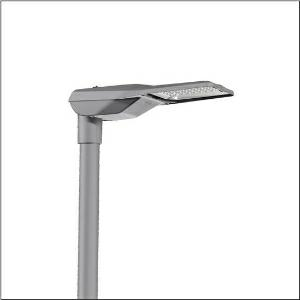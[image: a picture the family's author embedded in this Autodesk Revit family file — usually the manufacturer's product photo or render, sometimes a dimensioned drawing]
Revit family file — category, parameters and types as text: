
# Revit family: streetlight_sl_21_mini___p1_0a_5xe2a43s08gb_f3ee
name_source: partatom
category: Lighting Fixtures
units: mm (PartAtom-declared; Revit-internal decimal feet)

## family parameters
Cut with Voids When Loaded = No
Host = Face
Light Source = No
Part Type = Normal
Room Calculation Point = No
Round Connector Dimension = Use Diameter
Shared = No

## types (1)
- --- (1 x LED, 6180 lm, 40.4 W, 4000K)
    Apparent Load = 40 VA
    CIE Flux Codes = 21 50 90 100 100
    Color Rendering = 70
    Color Temperature = 4000K
    Default Elevation = 1800 mm
    Description = Streetlight SL 21 mini, mast luminaire, primary light control with lens, of PMMA, primary optical cover: cover, of toughened safety glass, transparent, light distribution: P1.0a, light emission: direct distribution, primary light characteristic: asymmetric, installation type: side-entry, post-top, LED, High Power LED, rated luminous flux: 6.180lm, luminous efficacy: 153lm/W, light colour: 740, colour temperature: 4000K, control gear: ECG Smart Interface, control: overheat protection, constant luminous flux control, time-dependent luminous flux control, flexible luminous flux parameterisation, mains connection: 220..240V, AC, 50/60Hz, start of lifetime: 40W, end of lifetime: 41W, reduction: 19W, luminaire housing, of diecast aluminium, powder-coated, Siteco® metallic grey (DB 702S), corrosivity category C5 according to DIN EN ISO 12944, length: 628mm, width: 235mm, height: 110mm, spigot size: 60/76mm (post-top) and 42/60/76mm (side-entry), mast flange for spigot size: 42mm: 5XC10008XM4, 60mm: 5XC10008XM2, 76/60mm: 5XC10108XM1, protection rating (complete): IP66, insulation class (complete): insulation class II (safety insulation), certification: CE, ENEC, VDE, impact resistance: IK09, permissible operating ambient temperature for outdoor applications: -40..+50°C, standard-compliant lighting for roads and squares, packaging unit: 1 piece

Light Distribution: P1.0a
    Height = 110 mm
    Lamp = 1 x LED
    Lamp Light Flux = 6180 lm
    Lamp Power = 40.4 W
    Lamp count = 1
    Length = 625 mm
    Luminous efficacy = 153 lm/W
    Manufacturer = Siteco
    ModVariant = No
    Model = 5XE2A43S08GB
    Number of Poles = 1
    OnlyDefault = Yes
    Power Factor = 1
    Product Name = Streetlight SL 21 mini | P1.0a
    Product group = mast luminaire | pylon top
    ProductGroupID = 6100
    Protection Class = Protection class II
    Protection Degree = IP 66
    RLX_Detail_Level = 1
    RlxData = <blob elided: 103117 chars, md5=4b16260f>
    Socket = socket
    Standby Power = 0 W
    System Light Flux = 6180 lm
    System Power = 40 W
    Type Comments = factory setting: luminous flux: 100 % | dim-lin: 254 | 812 mA
    Type Image = l_1003515.jpg
    URL = http://relux.com
    VarID = @adj_103735
    Voltage = 0 V
    Weight = 0.00 kg
    Width = 234 mm

## geometry (parser evidence)
native form markers: Blend x4, Sweep x12
no freeform markers — native parametric forms only
